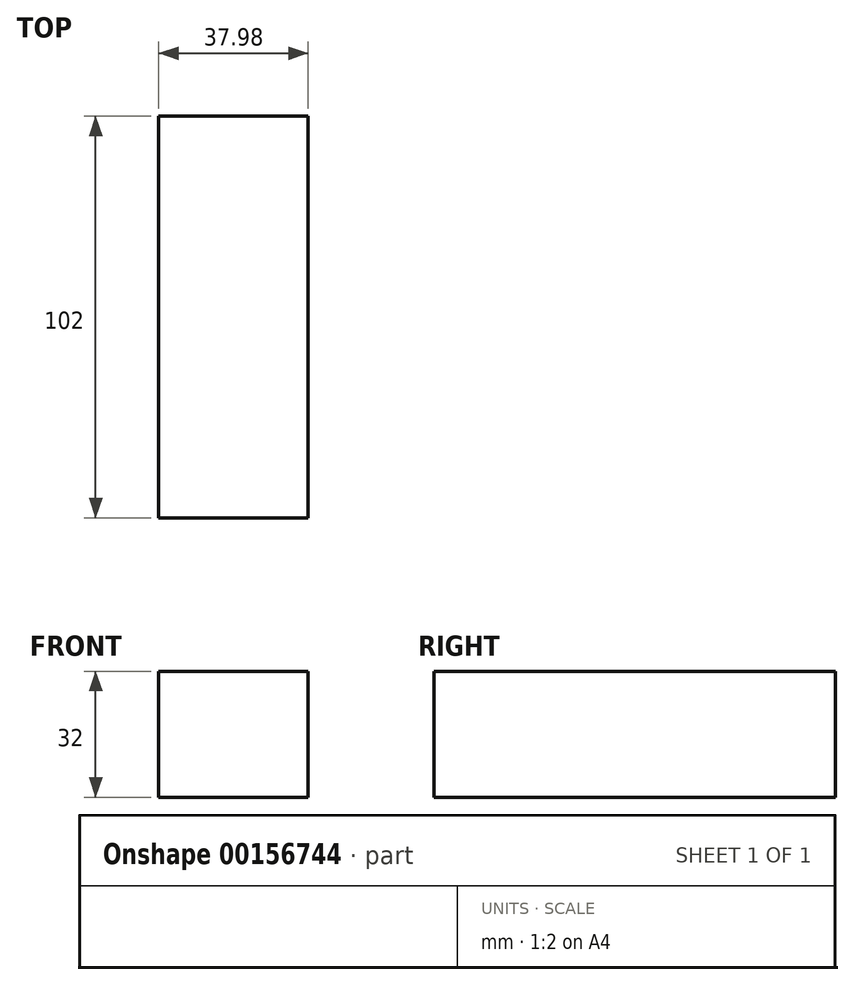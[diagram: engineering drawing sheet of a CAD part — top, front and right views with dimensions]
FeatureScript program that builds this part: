
annotation { "Feature Type Name" : "Feature", "Feature Type Description" : "" }
export const myFeature = defineFeature(function(context is Context, id is Id, definition is map)
    precondition{}
    {
        {
            var Q0;
            Q0=qCreatedBy(makeId("Front.planeOp"),FACE);
            var sketch = newSketch(context, id + "F0", { "sketchPlane" : qUnion([Q0])});
            skLineSegment(sketch, "E0.bottom", {"start": v(18.99, 16) * mm, "end": v(-18.99, 16) * mm});
            skLineSegment(sketch, "E0.top", {"start": v(18.99, -16) * mm, "end": v(-18.99, -16) * mm});
            skLineSegment(sketch, "E0.left", {"start": v(18.99, 16) * mm, "end": v(18.99, -16) * mm});
            skLineSegment(sketch, "E0.right", {"start": v(-18.99, 16) * mm, "end": v(-18.99, -16) * mm});
            skPoint(sketch, "E0.middle", {"position": v(0, 0) * mm});
            skSolve(sketch);
        }
        {
            var Q0;
            Q0 = qSketchRegion(id + "F0", true);
            extrude(context, id + "F1", {"entities" : qUnion([Q0]), "endBound" : BoundingType.SYMMETRIC, "depth" : 102 * mm});
        }
    });
